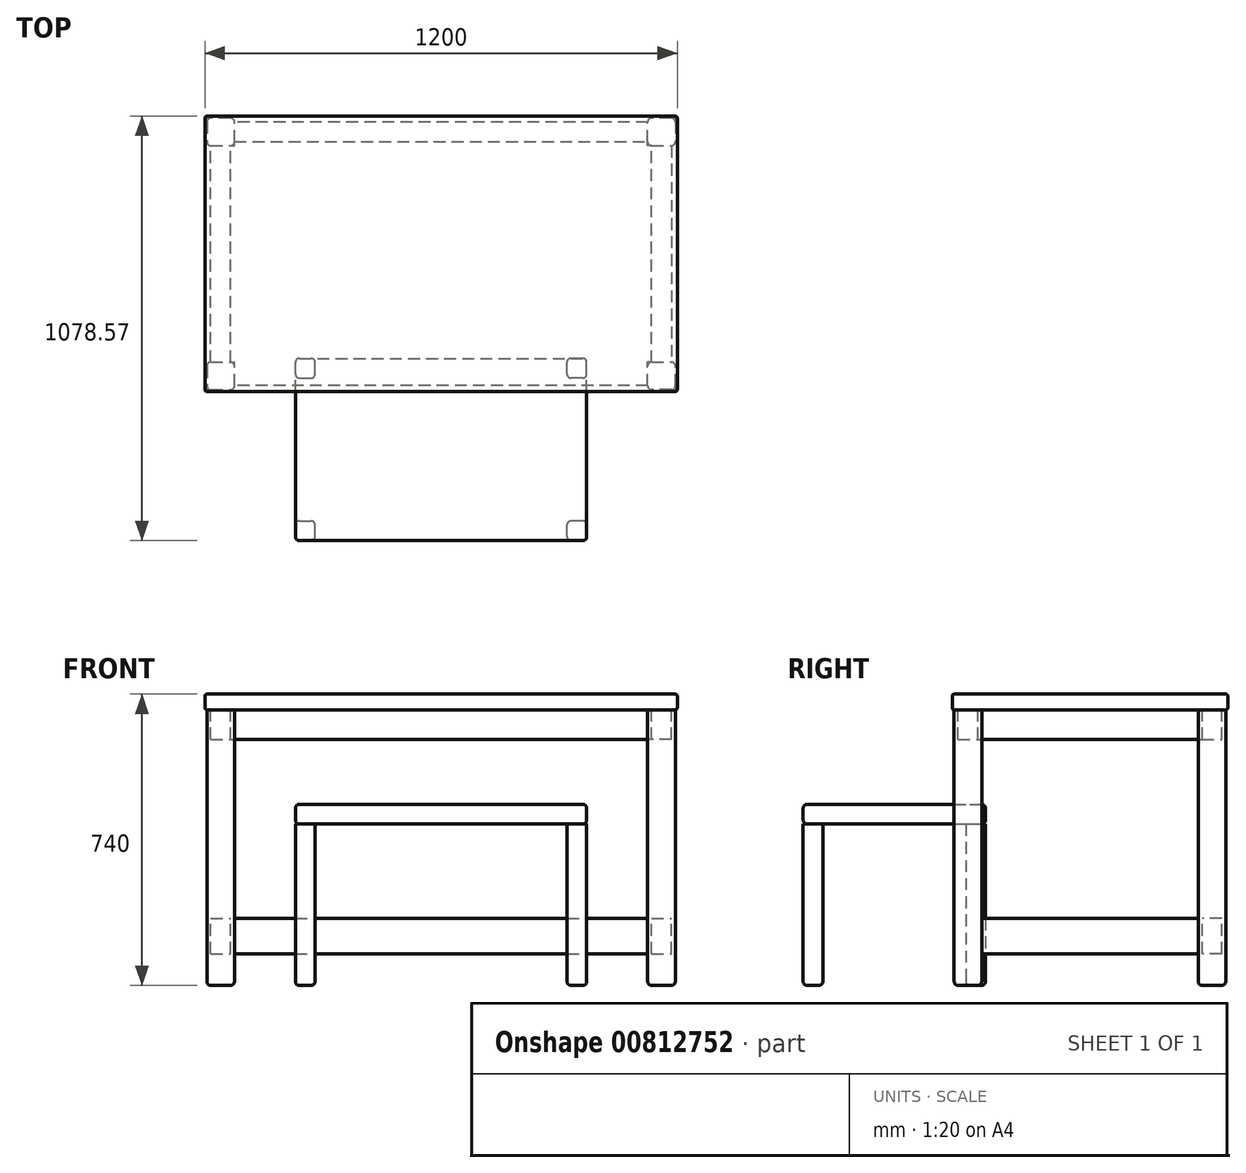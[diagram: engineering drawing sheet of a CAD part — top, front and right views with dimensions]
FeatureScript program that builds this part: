
annotation { "Feature Type Name" : "Feature", "Feature Type Description" : "" }
export const myFeature = defineFeature(function(context is Context, id is Id, definition is map)
    precondition{}
    {
        {
            var Q0;
            Q0=qCreatedBy(makeId("Top.planeOp"),FACE);
            var sketch = newSketch(context, id + "F0", { "sketchPlane" : qUnion([Q0])});
            skLineSegment(sketch, "E0.bottom", {"start": v(60, 35) * mm, "end": v(-60, 35) * mm});
            skLineSegment(sketch, "E0.top", {"start": v(60, -35) * mm, "end": v(-60, -35) * mm});
            skLineSegment(sketch, "E0.left", {"start": v(60, 35) * mm, "end": v(60, -35) * mm});
            skLineSegment(sketch, "E0.right", {"start": v(-60, 35) * mm, "end": v(-60, -35) * mm});
            skPoint(sketch, "E0.middle", {"position": v(0, 0) * mm});
            skSolve(sketch);
        }
        {
            var Q0;
            Q0 = qSketchRegion(id + "F0", true);
            extrude(context, id + "F1", {"entities" : qUnion([Q0]), "depth" : 4 * mm, "offsetDistance" : 25 * mm});
        }
        {
            var Q0;
            Q0=makeQuery(id+"F1.opExtrude","CAP_EDGE",EDGE,{"disambiguationData":[OSD([sQuery(id+"F0.wireOp",EDGE,"E0.right")])],"isStart":false});
            var Q1;
            Q1=makeQuery(id+"F1.opExtrude","CAP_EDGE",EDGE,{"disambiguationData":[OSD([sQuery(id+"F0.wireOp",EDGE,"E0.right")])],"isStart":true});
            var Q2;
            Q2=makeQuery(id+"F1.opExtrude","SWEPT_EDGE",EDGE,{"disambiguationData":[OSD([sQuery(id+"F0.wireOp",EDGE,"E0.top"),sQuery(id+"F0.wireOp",EDGE,"E0.right")])]});
            var Q3;
            Q3=makeQuery(id+"F1.opExtrude","CAP_EDGE",EDGE,{"disambiguationData":[OSD([sQuery(id+"F0.wireOp",EDGE,"E0.top")])],"isStart":true});
            var Q4;
            Q4=makeQuery(id+"F1.opExtrude","CAP_EDGE",EDGE,{"disambiguationData":[OSD([sQuery(id+"F0.wireOp",EDGE,"E0.top")])],"isStart":false});
            var Q5;
            Q5=makeQuery(id+"F1.opExtrude","SWEPT_EDGE",EDGE,{"disambiguationData":[OSD([sQuery(id+"F0.wireOp",EDGE,"E0.top"),sQuery(id+"F0.wireOp",EDGE,"E0.left")])]});
            var Q6;
            Q6=makeQuery(id+"F1.opExtrude","CAP_EDGE",EDGE,{"disambiguationData":[OSD([sQuery(id+"F0.wireOp",EDGE,"E0.left")])],"isStart":true});
            var Q7;
            Q7=makeQuery(id+"F1.opExtrude","CAP_EDGE",EDGE,{"disambiguationData":[OSD([sQuery(id+"F0.wireOp",EDGE,"E0.left")])],"isStart":false});
            var Q8;
            Q8=makeQuery(id+"F1.opExtrude","SWEPT_EDGE",EDGE,{"disambiguationData":[OSD([sQuery(id+"F0.wireOp",EDGE,"E0.bottom"),sQuery(id+"F0.wireOp",EDGE,"E0.left")])]});
            var Q9;
            Q9=makeQuery(id+"F1.opExtrude","CAP_EDGE",EDGE,{"disambiguationData":[OSD([sQuery(id+"F0.wireOp",EDGE,"E0.bottom")])],"isStart":false});
            var Q10;
            Q10=makeQuery(id+"F1.opExtrude","CAP_EDGE",EDGE,{"disambiguationData":[OSD([sQuery(id+"F0.wireOp",EDGE,"E0.bottom")])],"isStart":true});
            var Q11;
            Q11=makeQuery(id+"F1.opExtrude","SWEPT_EDGE",EDGE,{"disambiguationData":[OSD([sQuery(id+"F0.wireOp",EDGE,"E0.bottom"),sQuery(id+"F0.wireOp",EDGE,"E0.right")])]});
            fillet(context, id + "F2", {"entities" : qUnion([Q0, Q1, Q2, Q3, Q4, Q5, Q6, Q7, Q8, Q9, Q10, Q11]), "radius" : 0.5 * mm, "tangentPropagation" : true, "allowEdgeOverflow" : false});
        }
        {
            var Q0;
            Q0=qCreatedBy(makeId("Top.planeOp"),FACE);
            var sketch = newSketch(context, id + "F3", { "sketchPlane" : qUnion([Q0])});
            skLineSegment(sketch, "E1.bottom", {"start": v(-59.5, -34.5) * mm, "end": v(-52.5, -34.5) * mm});
            skLineSegment(sketch, "E1.top", {"start": v(-59.5, -27.5) * mm, "end": v(-52.5, -27.5) * mm});
            skLineSegment(sketch, "E1.left", {"start": v(-59.5, -34.5) * mm, "end": v(-59.5, -27.5) * mm});
            skLineSegment(sketch, "E1.right", {"start": v(-52.5, -34.5) * mm, "end": v(-52.5, -27.5) * mm});
            skLineSegment(sketch, "E2.bottom", {"start": v(59.5, -34.5) * mm, "end": v(52.5, -34.5) * mm});
            skLineSegment(sketch, "E2.top", {"start": v(59.5, -27.5) * mm, "end": v(52.5, -27.5) * mm});
            skLineSegment(sketch, "E2.left", {"start": v(59.5, -34.5) * mm, "end": v(59.5, -27.5) * mm});
            skLineSegment(sketch, "E2.right", {"start": v(52.5, -34.5) * mm, "end": v(52.5, -27.5) * mm});
            skLineSegment(sketch, "E3.bottom", {"start": v(59.5, 34.5) * mm, "end": v(52.5, 34.5) * mm});
            skLineSegment(sketch, "E3.top", {"start": v(59.5, 27.5) * mm, "end": v(52.5, 27.5) * mm});
            skLineSegment(sketch, "E3.left", {"start": v(59.5, 34.5) * mm, "end": v(59.5, 27.5) * mm});
            skLineSegment(sketch, "E3.right", {"start": v(52.5, 34.5) * mm, "end": v(52.5, 27.5) * mm});
            skLineSegment(sketch, "E4.bottom", {"start": v(-59.5, 34.5) * mm, "end": v(-52.5, 34.5) * mm});
            skLineSegment(sketch, "E4.top", {"start": v(-59.5, 27.5) * mm, "end": v(-52.5, 27.5) * mm});
            skLineSegment(sketch, "E4.left", {"start": v(-59.5, 34.5) * mm, "end": v(-59.5, 27.5) * mm});
            skLineSegment(sketch, "E4.right", {"start": v(-52.5, 34.5) * mm, "end": v(-52.5, 27.5) * mm});
            skSolve(sketch);
        }
        {
            var Q0;
            Q0 = qSketchRegion(id + "F3", true);
            extrude(context, id + "F4", {"entities" : qUnion([Q0]), "operationType" : NewBodyOperationType.ADD, "oppositeDirection" : true, "depth" : 70 * mm, "offsetDistance" : 25 * mm});
        }
        {
            var Q0;
            Q0=makeQuery(id+"F4.opExtrude","SWEPT_EDGE",EDGE,{"disambiguationData":[OSD([sQuery(id+"F3.wireOp",EDGE,"E1.bottom"),sQuery(id+"F3.wireOp",EDGE,"E1.left")])]});
            var Q1;
            Q1=makeQuery(id+"F4.opExtrude","SWEPT_EDGE",EDGE,{"disambiguationData":[OSD([sQuery(id+"F3.wireOp",EDGE,"E1.bottom"),sQuery(id+"F3.wireOp",EDGE,"E1.right")])]});
            var Q2;
            Q2=makeQuery(id+"F4.opExtrude","SWEPT_EDGE",EDGE,{"disambiguationData":[OSD([sQuery(id+"F3.wireOp",EDGE,"E1.top"),sQuery(id+"F3.wireOp",EDGE,"E1.left")])]});
            var Q3;
            Q3=makeQuery(id+"F4.opExtrude","SWEPT_EDGE",EDGE,{"disambiguationData":[OSD([sQuery(id+"F3.wireOp",EDGE,"E1.top"),sQuery(id+"F3.wireOp",EDGE,"E1.right")])]});
            var Q4;
            Q4=makeQuery(id+"F4.opExtrude","CAP_EDGE",EDGE,{"disambiguationData":[OSD([sQuery(id+"F3.wireOp",EDGE,"E1.left")])],"isStart":false});
            var Q5;
            Q5=makeQuery(id+"F4.opExtrude","CAP_EDGE",EDGE,{"disambiguationData":[OSD([sQuery(id+"F3.wireOp",EDGE,"E1.top")])],"isStart":false});
            var Q6;
            Q6=makeQuery(id+"F4.opExtrude","CAP_EDGE",EDGE,{"disambiguationData":[OSD([sQuery(id+"F3.wireOp",EDGE,"E1.right")])],"isStart":false});
            var Q7;
            Q7=makeQuery(id+"F4.opExtrude","CAP_EDGE",EDGE,{"disambiguationData":[OSD([sQuery(id+"F3.wireOp",EDGE,"E1.bottom")])],"isStart":false});
            var Q8;
            Q8=makeQuery(id+"F4.opExtrude","SWEPT_EDGE",EDGE,{"disambiguationData":[OSD([sQuery(id+"F3.wireOp",EDGE,"E2.bottom"),sQuery(id+"F3.wireOp",EDGE,"E2.left")])]});
            var Q9;
            Q9=makeQuery(id+"F4.opExtrude","SWEPT_EDGE",EDGE,{"disambiguationData":[OSD([sQuery(id+"F3.wireOp",EDGE,"E2.top"),sQuery(id+"F3.wireOp",EDGE,"E2.left")])]});
            var Q10;
            Q10=makeQuery(id+"F4.opExtrude","SWEPT_EDGE",EDGE,{"disambiguationData":[OSD([sQuery(id+"F3.wireOp",EDGE,"E2.bottom"),sQuery(id+"F3.wireOp",EDGE,"E2.right")])]});
            var Q11;
            Q11=makeQuery(id+"F4.opExtrude","SWEPT_EDGE",EDGE,{"disambiguationData":[OSD([sQuery(id+"F3.wireOp",EDGE,"E2.top"),sQuery(id+"F3.wireOp",EDGE,"E2.right")])]});
            var Q12;
            Q12=makeQuery(id+"F4.opExtrude","CAP_EDGE",EDGE,{"disambiguationData":[OSD([sQuery(id+"F3.wireOp",EDGE,"E2.bottom")])],"isStart":false});
            var Q13;
            Q13=makeQuery(id+"F4.opExtrude","CAP_EDGE",EDGE,{"disambiguationData":[OSD([sQuery(id+"F3.wireOp",EDGE,"E2.left")])],"isStart":false});
            var Q14;
            Q14=makeQuery(id+"F4.opExtrude","CAP_EDGE",EDGE,{"disambiguationData":[OSD([sQuery(id+"F3.wireOp",EDGE,"E2.top")])],"isStart":false});
            var Q15;
            Q15=makeQuery(id+"F4.opExtrude","CAP_EDGE",EDGE,{"disambiguationData":[OSD([sQuery(id+"F3.wireOp",EDGE,"E2.right")])],"isStart":false});
            var Q16;
            Q16=makeQuery(id+"F4.opExtrude","SWEPT_EDGE",EDGE,{"disambiguationData":[OSD([sQuery(id+"F3.wireOp",EDGE,"E3.bottom"),sQuery(id+"F3.wireOp",EDGE,"E3.left")])]});
            var Q17;
            Q17=makeQuery(id+"F4.opExtrude","SWEPT_EDGE",EDGE,{"disambiguationData":[OSD([sQuery(id+"F3.wireOp",EDGE,"E3.top"),sQuery(id+"F3.wireOp",EDGE,"E3.left")])]});
            var Q18;
            Q18=makeQuery(id+"F4.opExtrude","SWEPT_EDGE",EDGE,{"disambiguationData":[OSD([sQuery(id+"F3.wireOp",EDGE,"E3.bottom"),sQuery(id+"F3.wireOp",EDGE,"E3.right")])]});
            var Q19;
            Q19=makeQuery(id+"F4.opExtrude","SWEPT_EDGE",EDGE,{"disambiguationData":[OSD([sQuery(id+"F3.wireOp",EDGE,"E3.top"),sQuery(id+"F3.wireOp",EDGE,"E3.right")])]});
            var Q20;
            Q20=makeQuery(id+"F4.opExtrude","CAP_EDGE",EDGE,{"disambiguationData":[OSD([sQuery(id+"F3.wireOp",EDGE,"E3.top")])],"isStart":false});
            var Q21;
            Q21=makeQuery(id+"F4.opExtrude","CAP_EDGE",EDGE,{"disambiguationData":[OSD([sQuery(id+"F3.wireOp",EDGE,"E3.left")])],"isStart":false});
            var Q22;
            Q22=makeQuery(id+"F4.opExtrude","CAP_EDGE",EDGE,{"disambiguationData":[OSD([sQuery(id+"F3.wireOp",EDGE,"E3.bottom")])],"isStart":false});
            var Q23;
            Q23=makeQuery(id+"F4.opExtrude","CAP_EDGE",EDGE,{"disambiguationData":[OSD([sQuery(id+"F3.wireOp",EDGE,"E3.right")])],"isStart":false});
            var Q24;
            Q24=makeQuery(id+"F4.opExtrude","SWEPT_EDGE",EDGE,{"disambiguationData":[OSD([sQuery(id+"F3.wireOp",EDGE,"E4.top"),sQuery(id+"F3.wireOp",EDGE,"E4.left")])]});
            var Q25;
            Q25=makeQuery(id+"F4.opExtrude","SWEPT_EDGE",EDGE,{"disambiguationData":[OSD([sQuery(id+"F3.wireOp",EDGE,"E4.top"),sQuery(id+"F3.wireOp",EDGE,"E4.right")])]});
            var Q26;
            Q26=makeQuery(id+"F4.opExtrude","SWEPT_EDGE",EDGE,{"disambiguationData":[OSD([sQuery(id+"F3.wireOp",EDGE,"E4.bottom"),sQuery(id+"F3.wireOp",EDGE,"E4.left")])]});
            var Q27;
            Q27=makeQuery(id+"F4.opExtrude","SWEPT_EDGE",EDGE,{"disambiguationData":[OSD([sQuery(id+"F3.wireOp",EDGE,"E4.bottom"),sQuery(id+"F3.wireOp",EDGE,"E4.right")])]});
            var Q28;
            Q28=makeQuery(id+"F4.opExtrude","CAP_EDGE",EDGE,{"disambiguationData":[OSD([sQuery(id+"F3.wireOp",EDGE,"E4.right")])],"isStart":false});
            var Q29;
            Q29=makeQuery(id+"F4.opExtrude","CAP_EDGE",EDGE,{"disambiguationData":[OSD([sQuery(id+"F3.wireOp",EDGE,"E4.top")])],"isStart":false});
            var Q30;
            Q30=makeQuery(id+"F4.opExtrude","CAP_EDGE",EDGE,{"disambiguationData":[OSD([sQuery(id+"F3.wireOp",EDGE,"E4.bottom")])],"isStart":false});
            var Q31;
            Q31=makeQuery(id+"F4.opExtrude","CAP_EDGE",EDGE,{"disambiguationData":[OSD([sQuery(id+"F3.wireOp",EDGE,"E4.left")])],"isStart":false});
            fillet(context, id + "F5", {"entities" : qUnion([Q0, Q1, Q2, Q3, Q4, Q5, Q6, Q7, Q8, Q9, Q10, Q11, Q12, Q13, Q14, Q15, Q16, Q17, Q18, Q19, Q20, Q21, Q22, Q23, Q24, Q25, Q26, Q27, Q28, Q29, Q30, Q31]), "radius" : 1 * mm, "tangentPropagation" : true, "allowEdgeOverflow" : false});
        }
        {
            var Q0;
            Q0=makeQuery(id+"F4.opExtrude","SWEPT_FACE",FACE,{"disambiguationData":[OSD([sQuery(id+"F3.wireOp",EDGE,"E3.top")])]});
            var sketch = newSketch(context, id + "F6", { "sketchPlane" : qUnion([Q0])});
            skLineSegment(sketch, "E5.bottom", {"start": v(53.5, -62) * mm, "end": v(58.5, -62) * mm});
            skLineSegment(sketch, "E5.top", {"start": v(53.5, -53) * mm, "end": v(58.5, -53) * mm});
            skLineSegment(sketch, "E5.left", {"start": v(53.5, -62) * mm, "end": v(53.5, -53) * mm});
            skLineSegment(sketch, "E5.right", {"start": v(58.5, -62) * mm, "end": v(58.5, -53) * mm});
            skSolve(sketch);
        }
        {
            var Q0;
            Q0 = qSketchRegion(id + "F6", true);
            extrude(context, id + "F7", {"entities" : qUnion([Q0]), "operationType" : NewBodyOperationType.ADD, "depth" : 55 * mm, "offsetDistance" : 25 * mm});
        }
        {
            var Q0;
            Q0=makeQuery(id+"F4.opExtrude","SWEPT_FACE",FACE,{"disambiguationData":[OSD([sQuery(id+"F3.wireOp",EDGE,"E4.top")])]});
            var sketch = newSketch(context, id + "F8", { "sketchPlane" : qUnion([Q0])});
            skLineSegment(sketch, "E6.bottom", {"start": v(-58.5, -62) * mm, "end": v(-53.5, -62) * mm});
            skLineSegment(sketch, "E6.top", {"start": v(-58.5, -53) * mm, "end": v(-53.5, -53) * mm});
            skLineSegment(sketch, "E6.left", {"start": v(-58.5, -62) * mm, "end": v(-58.5, -53) * mm});
            skLineSegment(sketch, "E6.right", {"start": v(-53.5, -62) * mm, "end": v(-53.5, -53) * mm});
            skSolve(sketch);
        }
        {
            var Q0;
            Q0 = qSketchRegion(id + "F8", true);
            extrude(context, id + "F9", {"entities" : qUnion([Q0]), "operationType" : NewBodyOperationType.ADD, "depth" : 55 * mm, "offsetDistance" : 25 * mm});
        }
        {
            var Q0;
            Q0=makeQuery(id+"F4.opExtrude","SWEPT_FACE",FACE,{"disambiguationData":[OSD([sQuery(id+"F3.wireOp",EDGE,"E3.right")])]});
            var sketch = newSketch(context, id + "F10", { "sketchPlane" : qUnion([Q0])});
            skLineSegment(sketch, "E7.bottom", {"start": v(-33.5, -62) * mm, "end": v(-28.5, -62) * mm});
            skLineSegment(sketch, "E7.top", {"start": v(-33.5, -53) * mm, "end": v(-28.5, -53) * mm});
            skLineSegment(sketch, "E7.left", {"start": v(-33.5, -62) * mm, "end": v(-33.5, -53) * mm});
            skLineSegment(sketch, "E7.right", {"start": v(-28.5, -62) * mm, "end": v(-28.5, -53) * mm});
            skSolve(sketch);
        }
        {
            var Q0;
            Q0 = qSketchRegion(id + "F10", true);
            extrude(context, id + "F11", {"entities" : qUnion([Q0]), "operationType" : NewBodyOperationType.ADD, "depth" : 105 * mm, "offsetDistance" : 25 * mm});
        }
        {
            var Q0;
            Q0=makeQuery(id+"F4.opExtrude","SWEPT_FACE",FACE,{"disambiguationData":[OSD([sQuery(id+"F3.wireOp",EDGE,"E1.right")])]});
            var sketch = newSketch(context, id + "F12", { "sketchPlane" : qUnion([Q0])});
            skLineSegment(sketch, "E8.bottom", {"start": v(-33.5, -7.5) * mm, "end": v(33.5, -7.5) * mm});
            skLineSegment(sketch, "E8.top", {"start": v(-33.5, 0) * mm, "end": v(33.5, 0) * mm});
            skLineSegment(sketch, "E8.left", {"start": v(-33.5, -7.5) * mm, "end": v(-33.5, 0) * mm});
            skLineSegment(sketch, "E8.right", {"start": v(33.5, -7.5) * mm, "end": v(33.5, 0) * mm});
            skSolve(sketch);
        }
        {
            var Q0;
            Q0 = qSketchRegion(id + "F12", true);
            extrude(context, id + "F13", {"entities" : qUnion([Q0]), "operationType" : NewBodyOperationType.ADD, "depth" : 105 * mm, "offsetDistance" : 25 * mm});
        }
        {
            var Q0;
            {var subQ1=sQuery(id+"F3.wireOp",EDGE,"E2.top");Q0=makeQuery(id+"F7.boolean.opBoolean","SPLIT",FACE,{"disambiguationData":[TD([makeQuery(id+"F7.opExtrude","SWEPT_FACE",FACE,{"disambiguationData":[OSD([sQuery(id+"F6.wireOp",EDGE,"E5.top")])]})])],"derivedFrom":makeQuery(id+"F4.opExtrude","SWEPT_FACE",FACE,{"disambiguationData":[OSD([subQ1])]})});}
            var sketch = newSketch(context, id + "F14", { "sketchPlane" : qUnion([Q0])});
            skLineSegment(sketch, "E9.bottom", {"start": v(-58.5, -7.5) * mm, "end": v(-52.5, -7.5) * mm});
            skLineSegment(sketch, "E9.top", {"start": v(-58.5, 0) * mm, "end": v(-52.5, 0) * mm});
            skLineSegment(sketch, "E9.left", {"start": v(-58.5, -7.5) * mm, "end": v(-58.5, 0) * mm});
            skLineSegment(sketch, "E9.right", {"start": v(-52.5, -7.5) * mm, "end": v(-52.5, 0) * mm});
            skSolve(sketch);
        }
        {
            var Q0;
            Q0 = qSketchRegion(id + "F14", true);
            extrude(context, id + "F15", {"entities" : qUnion([Q0]), "operationType" : NewBodyOperationType.ADD, "depth" : 55 * mm, "offsetDistance" : 25 * mm});
        }
        {
            var Q0;
            {var subQ1=sQuery(id+"F3.wireOp",EDGE,"E4.top");Q0=makeQuery(id+"F9.boolean.opBoolean","SPLIT",FACE,{"disambiguationData":[TD([makeQuery(id+"F9.opExtrude","SWEPT_FACE",FACE,{"disambiguationData":[OSD([sQuery(id+"F8.wireOp",EDGE,"E6.top")])]})])],"derivedFrom":makeQuery(id+"F4.opExtrude","SWEPT_FACE",FACE,{"disambiguationData":[OSD([subQ1])]})});}
            var sketch = newSketch(context, id + "F16", { "sketchPlane" : qUnion([Q0])});
            skLineSegment(sketch, "E10.bottom", {"start": v(-58.5, -7.5) * mm, "end": v(-52.5, -7.5) * mm});
            skLineSegment(sketch, "E10.top", {"start": v(-58.5, 0) * mm, "end": v(-52.5, 0) * mm});
            skLineSegment(sketch, "E10.left", {"start": v(-58.5, -7.5) * mm, "end": v(-58.5, 0) * mm});
            skLineSegment(sketch, "E10.right", {"start": v(-52.5, -7.5) * mm, "end": v(-52.5, 0) * mm});
            skSolve(sketch);
        }
        {
            var Q0;
            Q0 = qSketchRegion(id + "F16", true);
            extrude(context, id + "F17", {"entities" : qUnion([Q0]), "operationType" : NewBodyOperationType.ADD, "depth" : 55 * mm, "offsetDistance" : 25 * mm});
        }
        {
            var Q0;
            Q0=makeQuery(id+"F1.opExtrude","SWEPT_BODY",BODY,{"disambiguationData":[OSD([sQuery(id+"F0.wireOp",EDGE,"E0.bottom"),sQuery(id+"F0.wireOp",EDGE,"E0.top"),sQuery(id+"F0.wireOp",EDGE,"E0.left"),sQuery(id+"F0.wireOp",EDGE,"E0.right")])]});
            var Q1;
            Q1=qCreatedBy(makeId("Origin.pointOp"),VERTEX);
            transform(context, id + "F18", {"entities" : qUnion([Q0]), "transformType" : TransformType.SCALE_UNIFORMLY, "scale" : 10, "scalePoint" : qUnion([Q1]), "makeCopy" : false});
        }
        {
            var Q0;
            Q0=makeQuery(id+"F4.opExtrude","CAP_FACE",FACE,{"disambiguationData":[OSD([sQuery(id+"F3.wireOp",EDGE,"E1.bottom"),sQuery(id+"F3.wireOp",EDGE,"E1.top"),sQuery(id+"F3.wireOp",EDGE,"E1.left"),sQuery(id+"F3.wireOp",EDGE,"E1.right")])],"isStart":false});
            var sketch = newSketch(context, id + "F19", { "sketchPlane" : qUnion([Q0])});
            skLineSegment(sketch, "E11.bottom", {"start": v(-370.07, 315.43) * mm, "end": v(-320.07, 315.43) * mm});
            skLineSegment(sketch, "E11.top", {"start": v(-370.07, 265.43) * mm, "end": v(-320.07, 265.43) * mm});
            skLineSegment(sketch, "E11.left", {"start": v(-370.07, 315.43) * mm, "end": v(-370.07, 265.43) * mm});
            skLineSegment(sketch, "E11.right", {"start": v(-320.07, 315.43) * mm, "end": v(-320.07, 265.43) * mm});
            skSolve(sketch);
        }
        {
            var Q0;
            Q0 = qSketchRegion(id + "F19", true);
            extrude(context, id + "F20", {"entities" : qUnion([Q0]), "oppositeDirection" : true, "depth" : 410 * mm, "offsetDistance" : 25 * mm});
        }
        {
            var Q0;
            Q0=makeQuery(id+"F20.opExtrude","SWEPT_BODY",BODY,{"disambiguationData":[OSD([sQuery(id+"F19.wireOp",EDGE,"E11.bottom"),sQuery(id+"F19.wireOp",EDGE,"E11.top"),sQuery(id+"F19.wireOp",EDGE,"E11.left"),sQuery(id+"F19.wireOp",EDGE,"E11.right")])]});
            var Q1;
            Q1=qCreatedBy(makeId("Right.planeOp"),FACE);
            mirror(context, id + "F21", {"entities" : qUnion([Q0]), "mirrorPlane" : qUnion([Q1])});
        }
        {
            var Q0;
            Q0=makeQuery(id+"F20.opExtrude","CAP_FACE",FACE,{"disambiguationData":[OSD([sQuery(id+"F19.wireOp",EDGE,"E11.bottom"),sQuery(id+"F19.wireOp",EDGE,"E11.top"),sQuery(id+"F19.wireOp",EDGE,"E11.left"),sQuery(id+"F19.wireOp",EDGE,"E11.right")])],"isStart":true});
            var sketch = newSketch(context, id + "F22", { "sketchPlane" : qUnion([Q0])});
            skLineSegment(sketch, "E12.bottom", {"start": v(-370.07, 528.57) * mm, "end": v(-320.07, 528.57) * mm});
            skLineSegment(sketch, "E12.top", {"start": v(-370.07, 478.57) * mm, "end": v(-320.07, 478.57) * mm});
            skLineSegment(sketch, "E12.left", {"start": v(-370.07, 528.57) * mm, "end": v(-370.07, 478.57) * mm});
            skLineSegment(sketch, "E12.right", {"start": v(-320.07, 528.57) * mm, "end": v(-320.07, 478.57) * mm});
            skSolve(sketch);
        }
        {
            var Q0;
            Q0 = qSketchRegion(id + "F22", true);
            extrude(context, id + "F23", {"entities" : qUnion([Q0]), "oppositeDirection" : true, "depth" : 410 * mm, "offsetDistance" : 25 * mm});
        }
        {
            var Q0;
            Q0=makeQuery(id+"F23.opExtrude","SWEPT_BODY",BODY,{"disambiguationData":[OSD([sQuery(id+"F22.wireOp",EDGE,"E12.bottom"),sQuery(id+"F22.wireOp",EDGE,"E12.top"),sQuery(id+"F22.wireOp",EDGE,"E12.left"),sQuery(id+"F22.wireOp",EDGE,"E12.right")])]});
            transform(context, id + "F24", {"entities" : qUnion([Q0]), "transformType" : TransformType.TRANSLATION_3D, "dx" : 0 * mm, "dy" : -200 * mm, "dz" : 0 * mm, "makeCopy" : false});
        }
        {
            var Q0;
            Q0=makeQuery(id+"F23.opExtrude","SWEPT_BODY",BODY,{"disambiguationData":[OSD([sQuery(id+"F22.wireOp",EDGE,"E12.bottom"),sQuery(id+"F22.wireOp",EDGE,"E12.top"),sQuery(id+"F22.wireOp",EDGE,"E12.left"),sQuery(id+"F22.wireOp",EDGE,"E12.right")])]});
            var Q1;
            Q1=qCreatedBy(makeId("Right.planeOp"),FACE);
            mirror(context, id + "F25", {"entities" : qUnion([Q0]), "mirrorPlane" : qUnion([Q1])});
        }
        {
            var Q0;
            Q0=makeQuery(id+"F23.opExtrude","CAP_FACE",FACE,{"disambiguationData":[OSD([sQuery(id+"F22.wireOp",EDGE,"E12.bottom"),sQuery(id+"F22.wireOp",EDGE,"E12.top"),sQuery(id+"F22.wireOp",EDGE,"E12.left"),sQuery(id+"F22.wireOp",EDGE,"E12.right")])],"isStart":false});
            var sketch = newSketch(context, id + "F26", { "sketchPlane" : qUnion([Q0])});
            skLineSegment(sketch, "E13.bottom", {"start": v(-370.07, -728.57) * mm, "end": v(370.04, -728.57) * mm});
            skLineSegment(sketch, "E13.top", {"start": v(-370.07, -265.45) * mm, "end": v(370.04, -265.45) * mm});
            skLineSegment(sketch, "E13.left", {"start": v(-370.07, -728.57) * mm, "end": v(-370.07, -265.45) * mm});
            skLineSegment(sketch, "E13.right", {"start": v(370.04, -728.57) * mm, "end": v(370.04, -265.45) * mm});
            skSolve(sketch);
        }
        {
            var Q0;
            Q0 = qSketchRegion(id + "F26", true);
            extrude(context, id + "F27", {"entities" : qUnion([Q0]), "depth" : 50 * mm, "offsetDistance" : 25 * mm});
        }
        {
            var Q0;
            Q0=makeQuery(id+"F23.opExtrude","SWEPT_EDGE",EDGE,{"disambiguationData":[OSD([sQuery(id+"F22.wireOp",EDGE,"E12.bottom"),sQuery(id+"F22.wireOp",EDGE,"E12.left")])]});
            var Q1;
            Q1=makeQuery(id+"F23.opExtrude","SWEPT_EDGE",EDGE,{"disambiguationData":[OSD([sQuery(id+"F22.wireOp",EDGE,"E12.bottom"),sQuery(id+"F22.wireOp",EDGE,"E12.right")])]});
            var Q2;
            Q2=makeQuery(id+"F23.opExtrude","SWEPT_EDGE",EDGE,{"disambiguationData":[OSD([sQuery(id+"F22.wireOp",EDGE,"E12.top"),sQuery(id+"F22.wireOp",EDGE,"E12.right")])]});
            var Q3;
            Q3=makeQuery(id+"F23.opExtrude","SWEPT_EDGE",EDGE,{"disambiguationData":[OSD([sQuery(id+"F22.wireOp",EDGE,"E12.top"),sQuery(id+"F22.wireOp",EDGE,"E12.left")])]});
            var Q4;
            Q4=makeQuery(id+"F20.opExtrude","SWEPT_EDGE",EDGE,{"disambiguationData":[OSD([sQuery(id+"F19.wireOp",EDGE,"E11.top"),sQuery(id+"F19.wireOp",EDGE,"E11.left")])]});
            var Q5;
            Q5=makeQuery(id+"F20.opExtrude","SWEPT_EDGE",EDGE,{"disambiguationData":[OSD([sQuery(id+"F19.wireOp",EDGE,"E11.top"),sQuery(id+"F19.wireOp",EDGE,"E11.right")])]});
            var Q6;
            Q6=makeQuery(id+"F20.opExtrude","SWEPT_EDGE",EDGE,{"disambiguationData":[OSD([sQuery(id+"F19.wireOp",EDGE,"E11.bottom"),sQuery(id+"F19.wireOp",EDGE,"E11.left")])]});
            var Q7;
            Q7=makeQuery(id+"F20.opExtrude","SWEPT_EDGE",EDGE,{"disambiguationData":[OSD([sQuery(id+"F19.wireOp",EDGE,"E11.bottom"),sQuery(id+"F19.wireOp",EDGE,"E11.right")])]});
            var Q8;
            Q8=makeQuery(id+"F25.opPattern","COPY",EDGE,{"derivedFrom":makeQuery(id+"F23.opExtrude","SWEPT_EDGE",EDGE,{"disambiguationData":[OSD([sQuery(id+"F22.wireOp",EDGE,"E12.bottom"),sQuery(id+"F22.wireOp",EDGE,"E12.left")])]}),"instanceName":"1"});
            var Q9;
            Q9=makeQuery(id+"F25.opPattern","COPY",EDGE,{"derivedFrom":makeQuery(id+"F23.opExtrude","SWEPT_EDGE",EDGE,{"disambiguationData":[OSD([sQuery(id+"F22.wireOp",EDGE,"E12.top"),sQuery(id+"F22.wireOp",EDGE,"E12.left")])]}),"instanceName":"1"});
            var Q10;
            Q10=makeQuery(id+"F25.opPattern","COPY",EDGE,{"derivedFrom":makeQuery(id+"F23.opExtrude","SWEPT_EDGE",EDGE,{"disambiguationData":[OSD([sQuery(id+"F22.wireOp",EDGE,"E12.bottom"),sQuery(id+"F22.wireOp",EDGE,"E12.right")])]}),"instanceName":"1"});
            var Q11;
            Q11=makeQuery(id+"F25.opPattern","COPY",EDGE,{"derivedFrom":makeQuery(id+"F23.opExtrude","SWEPT_EDGE",EDGE,{"disambiguationData":[OSD([sQuery(id+"F22.wireOp",EDGE,"E12.top"),sQuery(id+"F22.wireOp",EDGE,"E12.right")])]}),"instanceName":"1"});
            var Q12;
            Q12=makeQuery(id+"F21.opPattern","COPY",EDGE,{"derivedFrom":makeQuery(id+"F20.opExtrude","SWEPT_EDGE",EDGE,{"disambiguationData":[OSD([sQuery(id+"F19.wireOp",EDGE,"E11.bottom"),sQuery(id+"F19.wireOp",EDGE,"E11.right")])]}),"instanceName":"1"});
            var Q13;
            Q13=makeQuery(id+"F21.opPattern","COPY",EDGE,{"derivedFrom":makeQuery(id+"F20.opExtrude","SWEPT_EDGE",EDGE,{"disambiguationData":[OSD([sQuery(id+"F19.wireOp",EDGE,"E11.bottom"),sQuery(id+"F19.wireOp",EDGE,"E11.left")])]}),"instanceName":"1"});
            var Q14;
            Q14=makeQuery(id+"F21.opPattern","COPY",EDGE,{"derivedFrom":makeQuery(id+"F20.opExtrude","SWEPT_EDGE",EDGE,{"disambiguationData":[OSD([sQuery(id+"F19.wireOp",EDGE,"E11.top"),sQuery(id+"F19.wireOp",EDGE,"E11.right")])]}),"instanceName":"1"});
            var Q15;
            Q15=makeQuery(id+"F21.opPattern","COPY",EDGE,{"derivedFrom":makeQuery(id+"F20.opExtrude","SWEPT_EDGE",EDGE,{"disambiguationData":[OSD([sQuery(id+"F19.wireOp",EDGE,"E11.top"),sQuery(id+"F19.wireOp",EDGE,"E11.left")])]}),"instanceName":"1"});
            var Q16;
            Q16=makeQuery(id+"F21.opPattern","COPY",EDGE,{"derivedFrom":makeQuery(id+"F20.opExtrude","CAP_EDGE",EDGE,{"disambiguationData":[OSD([sQuery(id+"F19.wireOp",EDGE,"E11.left")])],"isStart":true}),"instanceName":"1"});
            var Q17;
            Q17=makeQuery(id+"F21.opPattern","COPY",EDGE,{"derivedFrom":makeQuery(id+"F20.opExtrude","CAP_EDGE",EDGE,{"disambiguationData":[OSD([sQuery(id+"F19.wireOp",EDGE,"E11.top")])],"isStart":true}),"instanceName":"1"});
            var Q18;
            Q18=makeQuery(id+"F21.opPattern","COPY",EDGE,{"derivedFrom":makeQuery(id+"F20.opExtrude","CAP_EDGE",EDGE,{"disambiguationData":[OSD([sQuery(id+"F19.wireOp",EDGE,"E11.right")])],"isStart":true}),"instanceName":"1"});
            var Q19;
            Q19=makeQuery(id+"F21.opPattern","COPY",EDGE,{"derivedFrom":makeQuery(id+"F20.opExtrude","CAP_EDGE",EDGE,{"disambiguationData":[OSD([sQuery(id+"F19.wireOp",EDGE,"E11.bottom")])],"isStart":true}),"instanceName":"1"});
            var Q20;
            Q20=makeQuery(id+"F20.opExtrude","CAP_EDGE",EDGE,{"disambiguationData":[OSD([sQuery(id+"F19.wireOp",EDGE,"E11.right")])],"isStart":true});
            var Q21;
            Q21=makeQuery(id+"F20.opExtrude","CAP_EDGE",EDGE,{"disambiguationData":[OSD([sQuery(id+"F19.wireOp",EDGE,"E11.top")])],"isStart":true});
            var Q22;
            Q22=makeQuery(id+"F20.opExtrude","CAP_EDGE",EDGE,{"disambiguationData":[OSD([sQuery(id+"F19.wireOp",EDGE,"E11.bottom")])],"isStart":true});
            var Q23;
            Q23=makeQuery(id+"F20.opExtrude","CAP_EDGE",EDGE,{"disambiguationData":[OSD([sQuery(id+"F19.wireOp",EDGE,"E11.left")])],"isStart":true});
            var Q24;
            Q24=makeQuery(id+"F23.opExtrude","CAP_EDGE",EDGE,{"disambiguationData":[OSD([sQuery(id+"F22.wireOp",EDGE,"E12.bottom")])],"isStart":true});
            var Q25;
            Q25=makeQuery(id+"F23.opExtrude","CAP_EDGE",EDGE,{"disambiguationData":[OSD([sQuery(id+"F22.wireOp",EDGE,"E12.left")])],"isStart":true});
            var Q26;
            Q26=makeQuery(id+"F23.opExtrude","CAP_EDGE",EDGE,{"disambiguationData":[OSD([sQuery(id+"F22.wireOp",EDGE,"E12.top")])],"isStart":true});
            var Q27;
            Q27=makeQuery(id+"F23.opExtrude","CAP_EDGE",EDGE,{"disambiguationData":[OSD([sQuery(id+"F22.wireOp",EDGE,"E12.right")])],"isStart":true});
            var Q28;
            Q28=makeQuery(id+"F25.opPattern","COPY",EDGE,{"derivedFrom":makeQuery(id+"F23.opExtrude","CAP_EDGE",EDGE,{"disambiguationData":[OSD([sQuery(id+"F22.wireOp",EDGE,"E12.left")])],"isStart":true}),"instanceName":"1"});
            var Q29;
            Q29=makeQuery(id+"F25.opPattern","COPY",EDGE,{"derivedFrom":makeQuery(id+"F23.opExtrude","CAP_EDGE",EDGE,{"disambiguationData":[OSD([sQuery(id+"F22.wireOp",EDGE,"E12.bottom")])],"isStart":true}),"instanceName":"1"});
            var Q30;
            Q30=makeQuery(id+"F25.opPattern","COPY",EDGE,{"derivedFrom":makeQuery(id+"F23.opExtrude","CAP_EDGE",EDGE,{"disambiguationData":[OSD([sQuery(id+"F22.wireOp",EDGE,"E12.right")])],"isStart":true}),"instanceName":"1"});
            var Q31;
            Q31=makeQuery(id+"F25.opPattern","COPY",EDGE,{"derivedFrom":makeQuery(id+"F23.opExtrude","CAP_EDGE",EDGE,{"disambiguationData":[OSD([sQuery(id+"F22.wireOp",EDGE,"E12.top")])],"isStart":true}),"instanceName":"1"});
            var Q32;
            Q32=makeQuery(id+"F27.opExtrude","CAP_EDGE",EDGE,{"disambiguationData":[OSD([sQuery(id+"F26.wireOp",EDGE,"E13.bottom")])],"isStart":false});
            var Q33;
            Q33=makeQuery(id+"F27.opExtrude","CAP_EDGE",EDGE,{"disambiguationData":[OSD([sQuery(id+"F26.wireOp",EDGE,"E13.bottom")])],"isStart":true});
            var Q34;
            Q34=makeQuery(id+"F27.opExtrude","CAP_EDGE",EDGE,{"disambiguationData":[OSD([sQuery(id+"F26.wireOp",EDGE,"E13.right")])],"isStart":false});
            var Q35;
            Q35=makeQuery(id+"F27.opExtrude","CAP_EDGE",EDGE,{"disambiguationData":[OSD([sQuery(id+"F26.wireOp",EDGE,"E13.right")])],"isStart":true});
            var Q36;
            Q36=makeQuery(id+"F27.opExtrude","SWEPT_EDGE",EDGE,{"disambiguationData":[OSD([sQuery(id+"F26.wireOp",EDGE,"E13.bottom"),sQuery(id+"F26.wireOp",EDGE,"E13.right")])]});
            var Q37;
            Q37=makeQuery(id+"F27.opExtrude","CAP_EDGE",EDGE,{"disambiguationData":[OSD([sQuery(id+"F26.wireOp",EDGE,"E13.left")])],"isStart":false});
            var Q38;
            Q38=makeQuery(id+"F27.opExtrude","CAP_EDGE",EDGE,{"disambiguationData":[OSD([sQuery(id+"F26.wireOp",EDGE,"E13.left")])],"isStart":true});
            var Q39;
            Q39=makeQuery(id+"F27.opExtrude","SWEPT_EDGE",EDGE,{"disambiguationData":[OSD([sQuery(id+"F26.wireOp",EDGE,"E13.bottom"),sQuery(id+"F26.wireOp",EDGE,"E13.left")])]});
            var Q40;
            Q40=makeQuery(id+"F27.opExtrude","SWEPT_EDGE",EDGE,{"disambiguationData":[OSD([sQuery(id+"F26.wireOp",EDGE,"E13.top"),sQuery(id+"F26.wireOp",EDGE,"E13.left")])]});
            var Q41;
            Q41=makeQuery(id+"F27.opExtrude","CAP_EDGE",EDGE,{"disambiguationData":[OSD([sQuery(id+"F26.wireOp",EDGE,"E13.top")])],"isStart":false});
            var Q42;
            Q42=makeQuery(id+"F27.opExtrude","CAP_EDGE",EDGE,{"disambiguationData":[OSD([sQuery(id+"F26.wireOp",EDGE,"E13.top")])],"isStart":true});
            var Q43;
            Q43=makeQuery(id+"F27.opExtrude","SWEPT_EDGE",EDGE,{"disambiguationData":[OSD([sQuery(id+"F26.wireOp",EDGE,"E13.top"),sQuery(id+"F26.wireOp",EDGE,"E13.right")])]});
            fillet(context, id + "F28", {"entities" : qUnion([Q0, Q1, Q2, Q3, Q4, Q5, Q6, Q7, Q8, Q9, Q10, Q11, Q12, Q13, Q14, Q15, Q16, Q17, Q18, Q19, Q20, Q21, Q22, Q23, Q24, Q25, Q26, Q27, Q28, Q29, Q30, Q31, Q32, Q33, Q34, Q35, Q36, Q37, Q38, Q39, Q40, Q41, Q42, Q43]), "radius" : 10 * mm, "tangentPropagation" : true, "allowEdgeOverflow" : false});
        }
    });
